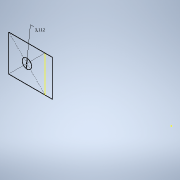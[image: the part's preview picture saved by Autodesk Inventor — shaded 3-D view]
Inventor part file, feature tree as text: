
AUTODESK INVENTOR PART (.ipt)
format: ipt  version: 2021 (Build 250183000, 183)  size: 100,864 bytes
history: native  units: mm
features: reference x5, other x3, extrude x1, sketch x1
ambient origin geometry x8: Origin, YZ Plane, XZ Plane, XY Plane, X Axis, Y Axis, Z Axis, Center Point
bodies: Volumenkörper1 (feature_tree)
feature tree (10):
  extrude  "Extrusion1"  Depth=6.0mm TaperAngle=0.0deg
  sketch  "Skizze1"  dims[d0=3.35mm d1=6.0mm d2=0.0mm]
  reference  "Referenz1"
  reference  "Referenz2"
  reference  "Referenz3"
  reference  "Referenz4"
  reference  "Referenz5"
  other  "<userpath>\Desktop\Bachelorarbeit\CAD\00_RobotAssembly.iam"
  other  "00_RobotAssembly.iam"
  other  "12_Motor_Fixation:1"
